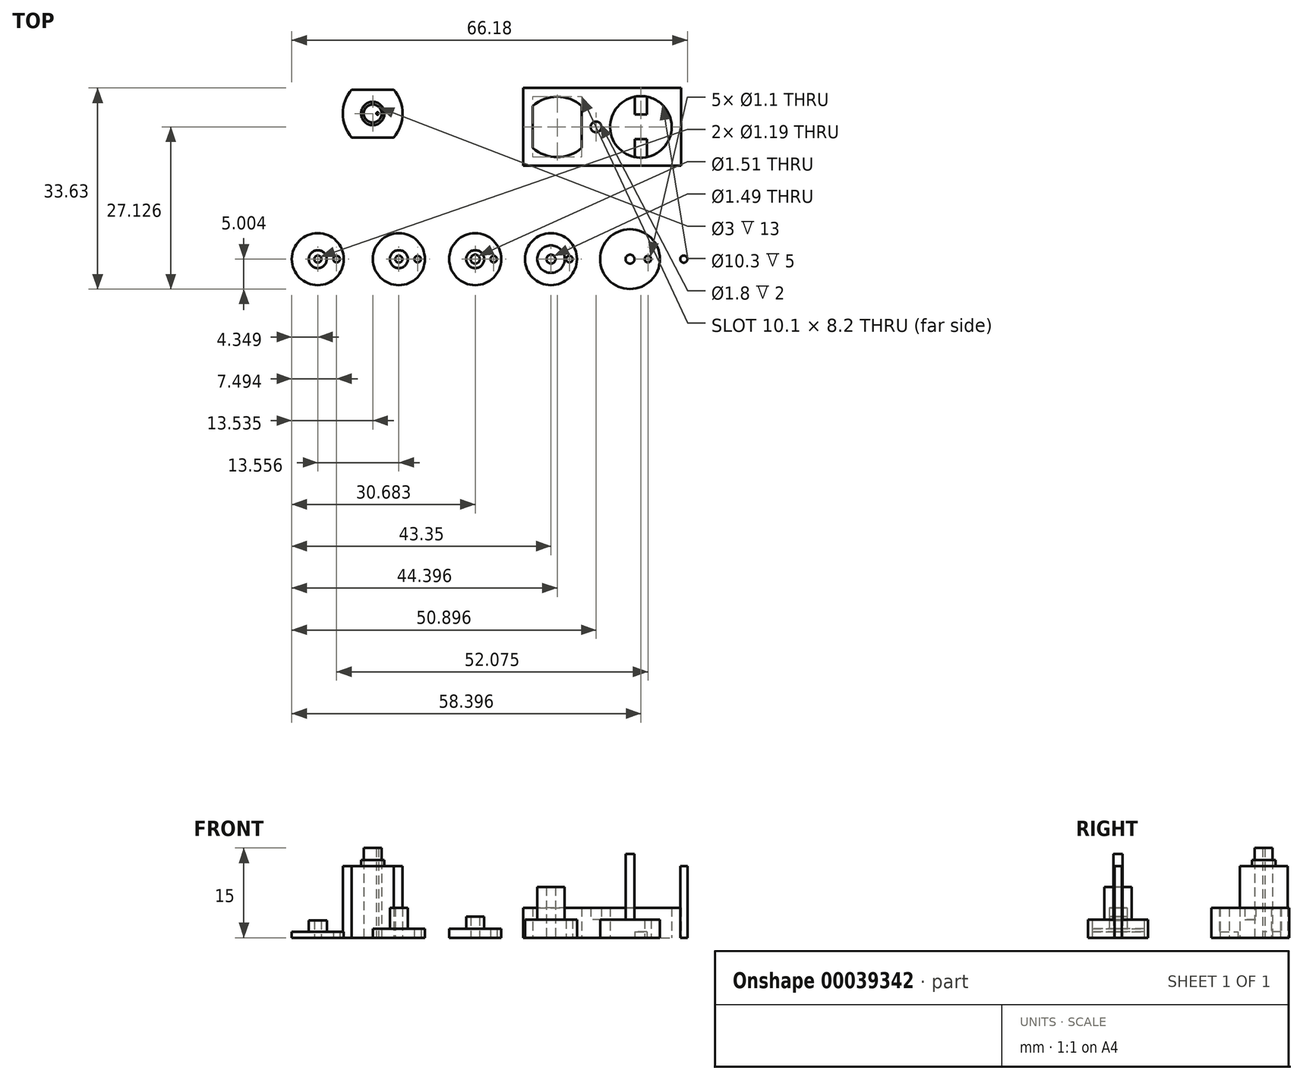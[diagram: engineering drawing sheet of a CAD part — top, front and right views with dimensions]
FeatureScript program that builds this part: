
annotation { "Feature Type Name" : "Feature", "Feature Type Description" : "" }
export const myFeature = defineFeature(function(context is Context, id is Id, definition is map)
    precondition{}
    {
        {
            var Q0;
            Q0=qCreatedBy(makeId("Top.planeOp"),FACE);
            var sketch = newSketch(context, id + "F0", { "sketchPlane" : qUnion([Q0])});
            skCircle(sketch, "E0", {"center": v(28.28, -7.3) * mm, "radius": 0.6 * mm});
            skCircle(sketch, "E1", {"center": v(-32.95, -7.3) * mm, "radius": 4.35 * mm});
            skCircle(sketch, "E2", {"center": v(-19.4, -7.3) * mm, "radius": 4.35 * mm});
            skCircle(sketch, "E3", {"center": v(-6.62, -7.3) * mm, "radius": 4.35 * mm});
            skCircle(sketch, "E4", {"center": v(6.05, -7.3) * mm, "radius": 4.35 * mm});
            skLineSegment(sketch, "E5", {"start": v(-43.4, -7.3) * mm, "end": v(45.72, -7.3) * mm, "construction": true});
            skCircle(sketch, "E6", {"center": v(19.27, -7.3) * mm, "radius": 0.75 * mm});
            skCircle(sketch, "E7", {"center": v(6.05, -7.3) * mm, "radius": 0.74 * mm});
            skCircle(sketch, "E8", {"center": v(-6.62, -7.3) * mm, "radius": 0.76 * mm});
            skCircle(sketch, "E9", {"center": v(-19.4, -7.3) * mm, "radius": 0.6 * mm});
            skCircle(sketch, "E10", {"center": v(-32.95, -7.3) * mm, "radius": 0.6 * mm});
            skCircle(sketch, "E11", {"center": v(6.05, -7.3) * mm, "radius": 2.3 * mm});
            skCircle(sketch, "E12", {"center": v(-6.62, -7.3) * mm, "radius": 1.5 * mm});
            skCircle(sketch, "E13", {"center": v(-19.4, -7.3) * mm, "radius": 1.5 * mm});
            skCircle(sketch, "E14", {"center": v(-32.95, -7.3) * mm, "radius": 1.5 * mm});
            skLineSegment(sketch, "E15.bottom", {"start": v(1.4, 21.33) * mm, "end": v(27.85, 21.33) * mm});
            skLineSegment(sketch, "E15.top", {"start": v(1.4, 8.33) * mm, "end": v(27.85, 8.33) * mm});
            skLineSegment(sketch, "E15.left", {"start": v(1.4, 21.33) * mm, "end": v(1.4, 8.33) * mm});
            skLineSegment(sketch, "E15.right", {"start": v(27.85, 21.33) * mm, "end": v(27.85, 8.33) * mm});
            skLineSegment(sketch, "E16", {"start": v(1.4, 14.83) * mm, "end": v(27.85, 14.83) * mm, "construction": true});
            skCircle(sketch, "E17", {"center": v(21.1, 14.83) * mm, "radius": 5.15 * mm});
            skCircle(sketch, "E18", {"center": v(13.6, 14.83) * mm, "radius": 0.9 * mm});
            skCircle(sketch, "E19", {"center": v(7.1, 14.83) * mm, "radius": 2 * mm});
            skCircle(sketch, "E20", {"center": v(-29.8, -7.3) * mm, "radius": 0.55 * mm});
            skCircle(sketch, "E21", {"center": v(-16.25, -7.3) * mm, "radius": 0.55 * mm});
            skCircle(sketch, "E22", {"center": v(-3.53, -7.3) * mm, "radius": 0.55 * mm});
            skCircle(sketch, "E23", {"center": v(9.13, -7.3) * mm, "radius": 0.55 * mm});
            skCircle(sketch, "E24", {"center": v(22.27, -7.3) * mm, "radius": 0.55 * mm});
            skLineSegment(sketch, "E25.bottom", {"start": v(-27.26, 21.06) * mm, "end": v(-20.26, 21.06) * mm});
            skLineSegment(sketch, "E25.top", {"start": v(-27.26, 13.06) * mm, "end": v(-20.26, 13.06) * mm});
            skLineSegment(sketch, "E26", {"start": v(-23.76, 21.06) * mm, "end": v(-23.76, 13.06) * mm, "construction": true});
            skLineSegment(sketch, "E27", {"start": v(-28.76, 17.06) * mm, "end": v(-18.76, 17.06) * mm, "construction": true});
            skLineSegment(sketch, "E28", {"start": v(-20.26, 21.06) * mm, "end": v(-20.26, 13.06) * mm, "construction": true});
            skLineSegment(sketch, "E29", {"start": v(-27.26, 21.06) * mm, "end": v(-27.26, 13.06) * mm, "construction": true});
            skCircle(sketch, "E30", {"center": v(-23.76, 17.06) * mm, "radius": 1.5 * mm});
            skCircle(sketch, "E31", {"center": v(-23.76, 17.06) * mm, "radius": 1.95 * mm});
            skArc(sketch, "E32", {"start": v(-20.26, 13.06) * mm, "mid": v(-18.76, 17.06) * mm, "end": v(-20.26, 21.06) * mm});
            skArc(sketch, "E33", {"start": v(-27.26, 21.06) * mm, "mid": v(-28.76, 17.06) * mm, "end": v(-27.26, 13.06) * mm});
            skLineSegment(sketch, "E34", {"start": v(7.1, 14.83) * mm, "end": v(7.1, 19.88) * mm, "construction": true});
            skLineSegment(sketch, "E35", {"start": v(7.1, 14.83) * mm, "end": v(7.1, 9.78) * mm, "construction": true});
            skPoint(sketch, "E36", {"position": v(3, 14.83) * mm});
            skPoint(sketch, "E37", {"position": v(11.2, 14.83) * mm});
            skPoint(sketch, "E38", {"position": v(7.1, 18.33) * mm});
            skPoint(sketch, "E39", {"position": v(7.1, 11.33) * mm});
            skLineSegment(sketch, "E40.bottom", {"start": v(3, 18.33) * mm, "end": v(11.2, 18.33) * mm, "construction": true});
            skLineSegment(sketch, "E40.top", {"start": v(3, 11.33) * mm, "end": v(11.2, 11.33) * mm, "construction": true});
            skLineSegment(sketch, "E41", {"start": v(3, 18.33) * mm, "end": v(3, 14.83) * mm});
            skLineSegment(sketch, "E42", {"start": v(3, 11.33) * mm, "end": v(3, 14.83) * mm});
            skLineSegment(sketch, "E43", {"start": v(11.2, 18.33) * mm, "end": v(11.2, 14.83) * mm});
            skLineSegment(sketch, "E44", {"start": v(11.2, 11.33) * mm, "end": v(11.2, 14.83) * mm});
            skArc(sketch, "E45", {"start": v(11.2, 18.33) * mm, "mid": v(7.1, 19.88) * mm, "end": v(3, 18.33) * mm});
            skArc(sketch, "E46", {"start": v(3, 11.33) * mm, "mid": v(7.1, 9.78) * mm, "end": v(11.2, 11.33) * mm});
            skCircle(sketch, "E47", {"center": v(-22.96, 17.06) * mm, "radius": 0.2 * mm});
            skCircle(sketch, "E48", {"center": v(19.27, -7.3) * mm, "radius": 5 * mm});
            skPoint(sketch, "E49", {"position": v(14.5, 14.83) * mm});
            skPoint(sketch, "E50", {"position": v(15.95, 14.83) * mm});
            skLineSegment(sketch, "E51", {"start": v(21.1, 19.98) * mm, "end": v(21.1, 9.68) * mm, "construction": true});
            skLineSegment(sketch, "E52", {"start": v(20.1, 9.77) * mm, "end": v(20.1, 12.77) * mm});
            skLineSegment(sketch, "E53", {"start": v(20.1, 12.77) * mm, "end": v(22.1, 12.77) * mm});
            skLineSegment(sketch, "E54", {"start": v(22.1, 12.77) * mm, "end": v(22.1, 9.77) * mm});
            skLineSegment(sketch, "E55", {"start": v(20.1, 19.88) * mm, "end": v(20.1, 16.88) * mm});
            skLineSegment(sketch, "E56", {"start": v(20.1, 16.88) * mm, "end": v(22.1, 16.88) * mm});
            skLineSegment(sketch, "E57", {"start": v(22.1, 16.88) * mm, "end": v(22.1, 19.88) * mm});
            skPoint(sketch, "E58", {"position": v(12.7, 14.83) * mm});
            skSolve(sketch);
        }
        {
            var Q0;
            Q0=makeQuery(id+"F0.imprint","IMPRINT",FACE,{"disambiguationData":[TD([[makeQuery(id+"F0.imprint","IMPRINT",EDGE,{"derivedFrom":sQuery(id+"F0.wireOp",EDGE,"E6")}),-1.0]])]});
            extrude(context, id + "F1", {"entities" : qUnion([Q0]), "depth" : 3 * mm});
        }
        {
            var Q0;
            Q0=makeQuery(id+"F0.imprint","IMPRINT",FACE,{"disambiguationData":[TD([[makeQuery(id+"F0.imprint","IMPRINT",EDGE,{"derivedFrom":sQuery(id+"F0.wireOp",EDGE,"E6")}),1.0]])]});
            extrude(context, id + "F2", {"entities" : qUnion([Q0]), "operationType" : NewBodyOperationType.ADD, "depth" : 14 * mm});
        }
        {
            var Q0;
            Q0=makeQuery(id+"F0.imprint","IMPRINT",FACE,{"disambiguationData":[TD([[makeQuery(id+"F0.imprint","IMPRINT",EDGE,{"derivedFrom":sQuery(id+"F0.wireOp",EDGE,"E4")}),1.0]])]});
            extrude(context, id + "F3", {"entities" : qUnion([Q0]), "depth" : 3 * mm});
        }
        {
            var Q0;
            Q0=makeQuery(id+"F0.imprint","IMPRINT",FACE,{"disambiguationData":[TD([[makeQuery(id+"F0.imprint","IMPRINT",EDGE,{"derivedFrom":sQuery(id+"F0.wireOp",EDGE,"E7")}),-1.0]])]});
            extrude(context, id + "F4", {"entities" : qUnion([Q0]), "operationType" : NewBodyOperationType.ADD, "depth" : 8.5 * mm});
        }
        {
            var Q0;
            Q0=makeQuery(id+"F0.imprint","IMPRINT",FACE,{"disambiguationData":[TD([[makeQuery(id+"F0.imprint","IMPRINT",EDGE,{"derivedFrom":sQuery(id+"F0.wireOp",EDGE,"E3")}),1.0]])]});
            extrude(context, id + "F5", {"entities" : qUnion([Q0]), "depth" : 1.5 * mm});
        }
        {
            var Q0;
            Q0=makeQuery(id+"F0.imprint","IMPRINT",FACE,{"disambiguationData":[TD([[makeQuery(id+"F0.imprint","IMPRINT",EDGE,{"derivedFrom":sQuery(id+"F0.wireOp",EDGE,"E8")}),-1.0]])]});
            extrude(context, id + "F6", {"entities" : qUnion([Q0]), "operationType" : NewBodyOperationType.ADD, "depth" : 3.5 * mm});
        }
        {
            var Q0;
            Q0=makeQuery(id+"F0.imprint","IMPRINT",FACE,{"disambiguationData":[TD([[makeQuery(id+"F0.imprint","IMPRINT",EDGE,{"derivedFrom":sQuery(id+"F0.wireOp",EDGE,"E2")}),1.0]])]});
            extrude(context, id + "F7", {"entities" : qUnion([Q0]), "depth" : 1.5 * mm});
        }
        {
            var Q0;
            Q0=makeQuery(id+"F0.imprint","IMPRINT",FACE,{"disambiguationData":[TD([[makeQuery(id+"F0.imprint","IMPRINT",EDGE,{"derivedFrom":sQuery(id+"F0.wireOp",EDGE,"E9")}),-1.0]])]});
            extrude(context, id + "F8", {"entities" : qUnion([Q0]), "operationType" : NewBodyOperationType.ADD, "depth" : 5 * mm});
        }
        {
            var Q0;
            Q0=makeQuery(id+"F0.imprint","IMPRINT",FACE,{"disambiguationData":[TD([[makeQuery(id+"F0.imprint","IMPRINT",EDGE,{"derivedFrom":sQuery(id+"F0.wireOp",EDGE,"E1")}),1.0]])]});
            extrude(context, id + "F9", {"entities" : qUnion([Q0]), "depth" : 1 * mm});
        }
        {
            var Q0;
            Q0=makeQuery(id+"F0.imprint","IMPRINT",FACE,{"disambiguationData":[TD([[makeQuery(id+"F0.imprint","IMPRINT",EDGE,{"derivedFrom":sQuery(id+"F0.wireOp",EDGE,"E10")}),-1.0]])]});
            extrude(context, id + "F10", {"entities" : qUnion([Q0]), "operationType" : NewBodyOperationType.ADD, "depth" : 2.9 * mm});
        }
        {
            var Q0;
            Q0=makeQuery(id+"F0.imprint","IMPRINT",FACE,{"disambiguationData":[TD([[makeQuery(id+"F0.imprint","IMPRINT",EDGE,{"derivedFrom":sQuery(id+"F0.wireOp",EDGE,"E0")}),1.0]])]});
            extrude(context, id + "F11", {"entities" : qUnion([Q0]), "depth" : 12 * mm});
        }
        {
            var Q0;
            Q0=makeQuery(id+"F0.imprint","IMPRINT",FACE,{"disambiguationData":[TD([[makeQuery(id+"F0.imprint","IMPRINT",EDGE,{"derivedFrom":sQuery(id+"F0.wireOp",EDGE,"E15.bottom")}),-1.0]])]});
            var Q1;
            {var subQ2=sQuery(id+"F0.wireOp",EDGE,"E15.left");Q1=makeQuery(id+"F0.imprint","IMPRINT",FACE,{"disambiguationData":[TD([[makeQuery(id+"F0.imprint","IMPRINT",EDGE,{"derivedFrom":subQ2}),1.0]])]});}
            extrude(context, id + "F12", {"entities" : qUnion([Q0, Q1]), "depth" : 6 * mm});
        }
        {
            var Q0;
            Q0=makeQuery(id+"F0.imprint","IMPRINT",FACE,{"disambiguationData":[TD([[makeQuery(id+"F0.imprint","IMPRINT",EDGE,{"derivedFrom":sQuery(id+"F0.wireOp",EDGE,"E18")}),1.0]])]});
            extrude(context, id + "F13", {"entities" : qUnion([Q0]), "operationType" : NewBodyOperationType.ADD, "depth" : 3 * mm});
        }
        {
            var Q0;
            {var subQ0=sQuery(id+"F0.wireOp",EDGE,"E55");Q0=makeQuery(id+"F0.imprint","IMPRINT",FACE,{"disambiguationData":[TD([[makeQuery(id+"F0.imprint","IMPRINT",EDGE,{"derivedFrom":subQ0}),1.0]])]});}
            var Q1;
            {var subQ1=sQuery(id+"F0.wireOp",EDGE,"E52");Q1=makeQuery(id+"F0.imprint","IMPRINT",FACE,{"disambiguationData":[TD([[makeQuery(id+"F0.imprint","IMPRINT",EDGE,{"derivedFrom":subQ1}),-1.0]])]});}
            extrude(context, id + "F14", {"entities" : qUnion([Q0, Q1]), "operationType" : NewBodyOperationType.ADD, "depth" : 1 * mm});
        }
        {
            var Q0;
            Q0=makeQuery(id+"F0.imprint","IMPRINT",FACE,{"disambiguationData":[TD([[makeQuery(id+"F0.imprint","IMPRINT",EDGE,{"derivedFrom":sQuery(id+"F0.wireOp",EDGE,"E19")}),-1.0]])]});
            extrude(context, id + "F15", {"entities" : qUnion([Q0]), "operationType" : NewBodyOperationType.REMOVE, "depth" : 5 * mm});
        }
        {
            var Q0;
            Q0=makeQuery(id+"F0.imprint","IMPRINT",FACE,{"disambiguationData":[TD([[makeQuery(id+"F0.imprint","IMPRINT",EDGE,{"derivedFrom":sQuery(id+"F0.wireOp",EDGE,"E25.bottom")}),-1.0]])]});
            extrude(context, id + "F16", {"entities" : qUnion([Q0]), "depth" : 12 * mm});
        }
        {
            var Q0;
            Q0=makeQuery(id+"F0.imprint","IMPRINT",FACE,{"disambiguationData":[TD([[makeQuery(id+"F0.imprint","IMPRINT",EDGE,{"derivedFrom":sQuery(id+"F0.wireOp",EDGE,"E30")}),-1.0]])]});
            extrude(context, id + "F17", {"entities" : qUnion([Q0]), "operationType" : NewBodyOperationType.ADD, "depth" : 13 * mm});
        }
        {
            var Q0;
            Q0=makeQuery(id+"F0.imprint","IMPRINT",FACE,{"disambiguationData":[TD([[makeQuery(id+"F0.imprint","IMPRINT",EDGE,{"derivedFrom":sQuery(id+"F0.wireOp",EDGE,"E30")}),1.0]])]});
            extrude(context, id + "F18", {"entities" : qUnion([Q0]), "depth" : 15 * mm});
        }
        {
            var Q0;
            Q0=makeQuery(id+"F12.opExtrude","CAP_FACE",FACE,{"disambiguationData":[OSD([sQuery(id+"F0.wireOp",EDGE,"E15.bottom"),sQuery(id+"F0.wireOp",EDGE,"E15.top"),sQuery(id+"F0.wireOp",EDGE,"E15.left"),sQuery(id+"F0.wireOp",EDGE,"E15.right"),sQuery(id+"F0.wireOp",EDGE,"E17"),sQuery(id+"F0.wireOp",EDGE,"E18"),sQuery(id+"F0.wireOp",EDGE,"E41"),sQuery(id+"F0.wireOp",EDGE,"E42"),sQuery(id+"F0.wireOp",EDGE,"E43"),sQuery(id+"F0.wireOp",EDGE,"E44"),sQuery(id+"F0.wireOp",EDGE,"E45"),sQuery(id+"F0.wireOp",EDGE,"E46")])],"isStart":false});
            extrude(context, id + "F19", {"entities" : qUnion([Q0]), "operationType" : NewBodyOperationType.REMOVE, "oppositeDirection" : true, "depth" : 1 * mm});
        }
    });
